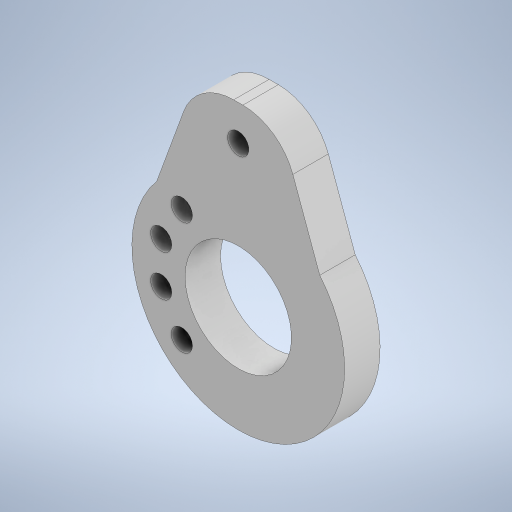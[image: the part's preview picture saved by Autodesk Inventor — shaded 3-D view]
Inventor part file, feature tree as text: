
AUTODESK INVENTOR PART (.ipt)
format: ipt  version: 2024.3 (Build 283343000, 343)  size: 309,760 bytes
history: native  units: mm
features: sketch x3, extrude x2, hole x1, fillet x1
ambient origin geometry x8: Origin, YZ Plane, XZ Plane, XY Plane, X Axis, Y Axis, Z Axis, Center Point
bodies: Body1 (feature_tree)
feature tree (7):
  extrude  "押し出し2"  Depth=60.0mm
  hole  "穴1"  [1 undecoded]
  extrude  "押し出し3"  Depth=12.217305mm
  fillet  "フィレット2"  Radius=12.217305mm
  sketch  "スケッチ12"
  sketch  "スケッチ13"
  sketch  "スケッチ14"
note: 1 required parameter value undecoded (feature->parameter linkage not recoverable at this tier; creation-order binding heuristic only, values carry confidence <= 0.55)
